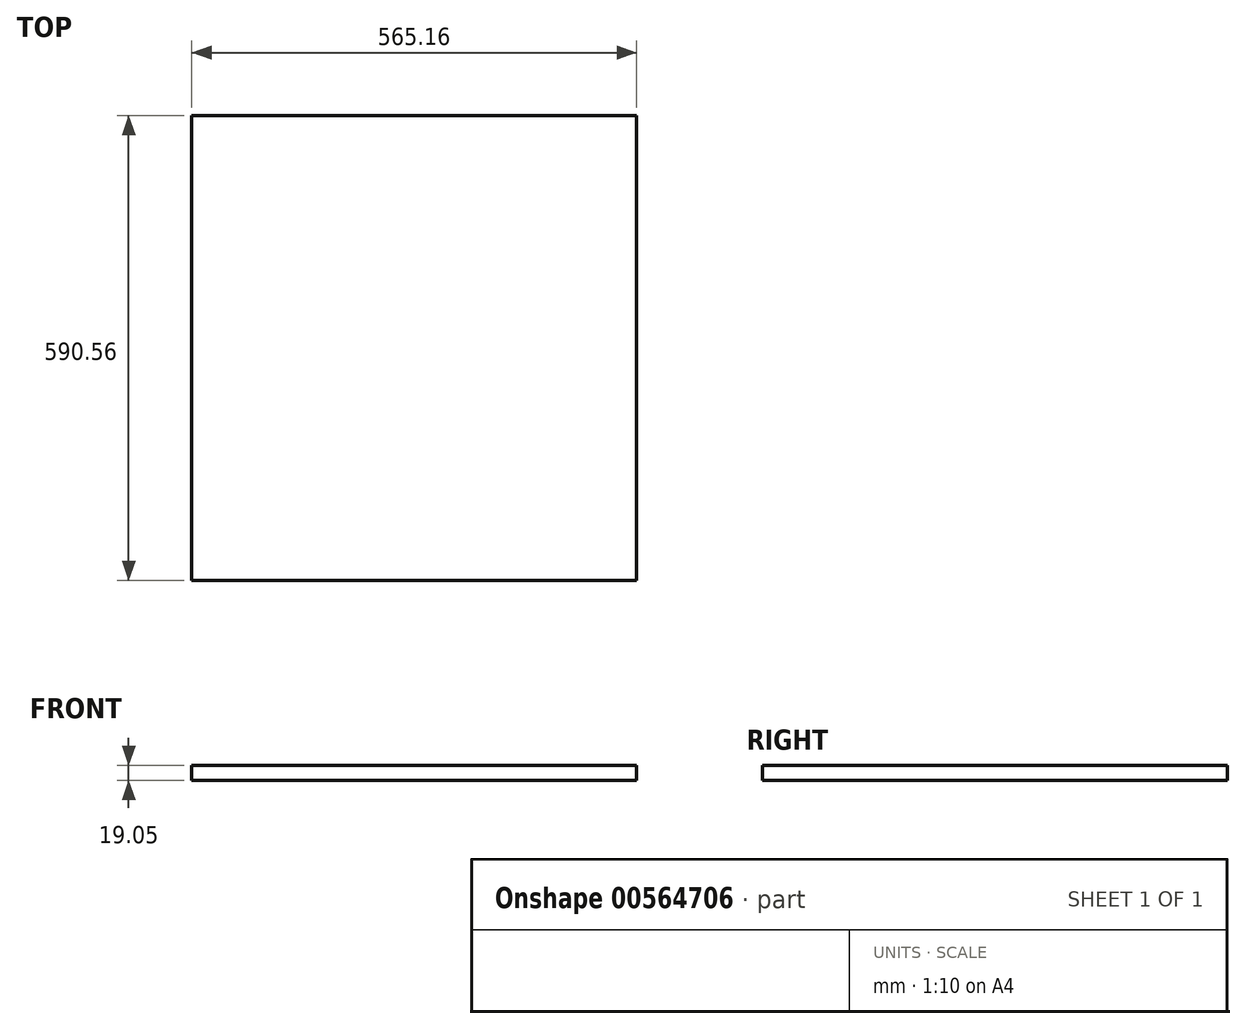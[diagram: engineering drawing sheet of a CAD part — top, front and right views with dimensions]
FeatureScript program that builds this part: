
annotation { "Feature Type Name" : "Feature", "Feature Type Description" : "" }
export const myFeature = defineFeature(function(context is Context, id is Id, definition is map)
    precondition{}
    {
        {
            var Q0;
            Q0=qCreatedBy(makeId("Top.planeOp"),FACE);
            var sketch = newSketch(context, id + "F0", { "sketchPlane" : qUnion([Q0])});
            skLineSegment(sketch, "E0.bottom", {"start": v(282.58, -295.28) * mm, "end": v(-282.58, -295.28) * mm});
            skLineSegment(sketch, "E0.top", {"start": v(282.58, 295.28) * mm, "end": v(-282.58, 295.27) * mm});
            skLineSegment(sketch, "E0.left", {"start": v(282.58, -295.28) * mm, "end": v(282.58, 295.28) * mm});
            skLineSegment(sketch, "E0.right", {"start": v(-282.58, -295.28) * mm, "end": v(-282.58, 295.27) * mm});
            skPoint(sketch, "E0.middle", {"position": v(0, 0) * mm});
            skSolve(sketch);
        }
        {
            var Q0;
            Q0=makeQuery(id+"F0.imprint","IMPRINT",FACE,{"disambiguationData":[TD([[makeQuery(id+"F0.imprint","IMPRINT",EDGE,{"derivedFrom":sQuery(id+"F0.wireOp",EDGE,"E0.bottom")}),-1.0]])]});
            extrude(context, id + "F1", {"entities" : qUnion([Q0]), "depth" : 19.05 * mm, "offsetDistance" : 25.4 * mm});
        }
    });
